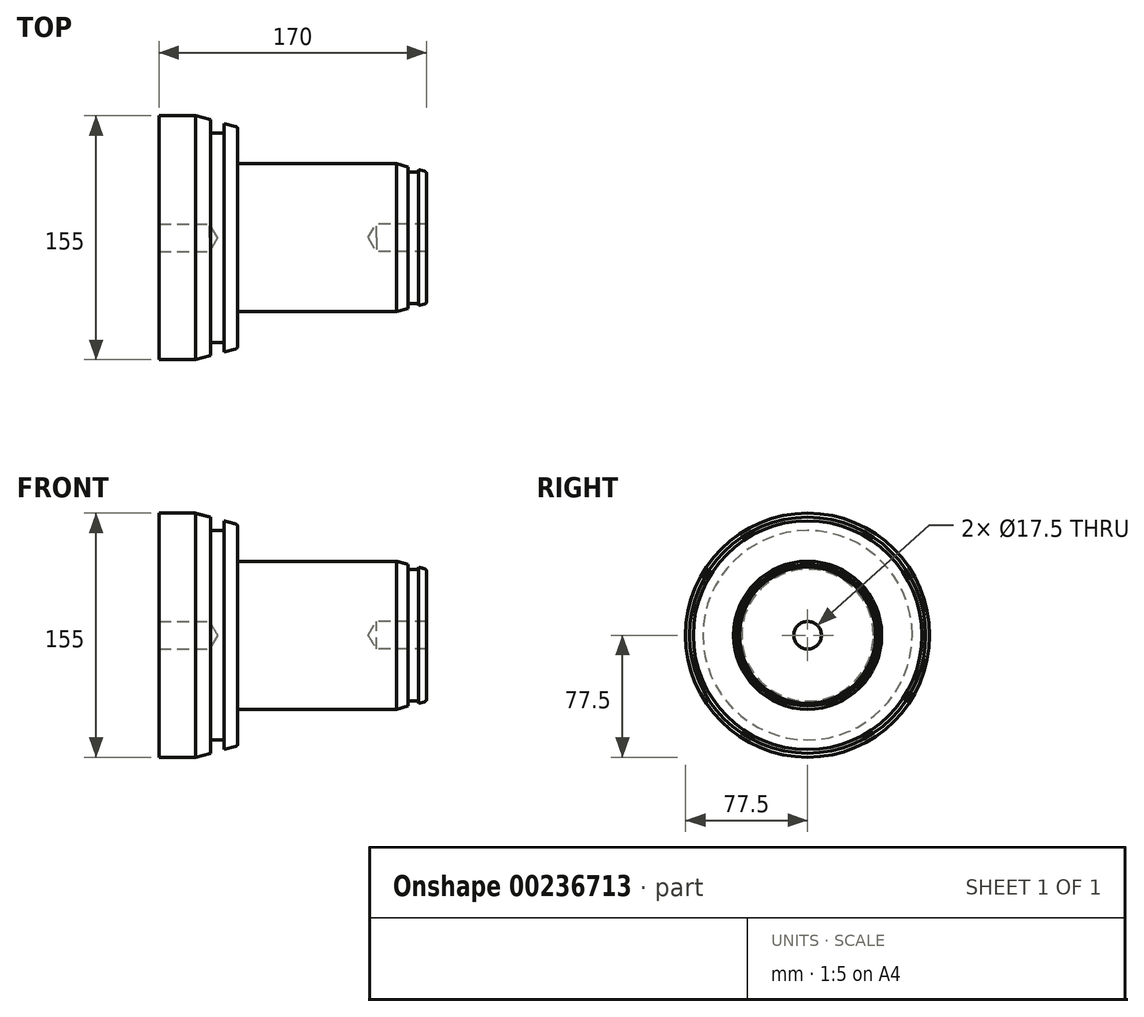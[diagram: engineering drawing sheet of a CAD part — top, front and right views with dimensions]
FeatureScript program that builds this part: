
annotation { "Feature Type Name" : "Feature", "Feature Type Description" : "" }
export const myFeature = defineFeature(function(context is Context, id is Id, definition is map)
    precondition{}
    {
        {
            var Q0;
            Q0=qCreatedBy(makeId("Front.planeOp"),FACE);
            var sketch = newSketch(context, id + "F0", { "sketchPlane" : qUnion([Q0])});
            skLineSegment(sketch, "E0", {"start": v(0, 0) * mm, "end": v(170, 0) * mm});
            skLineSegment(sketch, "E1", {"start": v(0, 0) * mm, "end": v(0, 77.5) * mm});
            skLineSegment(sketch, "E2", {"start": v(0, 77.5) * mm, "end": v(23.18, 77.5) * mm});
            skLineSegment(sketch, "E3", {"start": v(23.18, 77.5) * mm, "end": v(32.6, 74.98) * mm});
            skLineSegment(sketch, "E4", {"start": v(50, 68.78) * mm, "end": v(50, 48) * mm});
            skLineSegment(sketch, "E5", {"start": v(51, 47) * mm, "end": v(150.74, 47) * mm});
            skLineSegment(sketch, "E6", {"start": v(158.25, 44.99) * mm, "end": v(158.25, 41.84) * mm});
            skLineSegment(sketch, "E7", {"start": v(158.25, 41.84) * mm, "end": v(164.75, 41.84) * mm});
            skLineSegment(sketch, "E8", {"start": v(164.75, 41.84) * mm, "end": v(164.75, 43.25) * mm});
            skLineSegment(sketch, "E9", {"start": v(170, 40.3) * mm, "end": v(170, 0) * mm});
            skLineSegment(sketch, "E10", {"start": v(41.4, 72.62) * mm, "end": v(41.4, 66.46) * mm});
            skLineSegment(sketch, "E11", {"start": v(41.4, 66.46) * mm, "end": v(32.6, 66.46) * mm});
            skLineSegment(sketch, "E12", {"start": v(32.6, 66.46) * mm, "end": v(32.6, 74.98) * mm});
            skLineSegment(sketch, "E13.trimOffspring", {"start": v(41.4, 72.62) * mm, "end": v(48.52, 70.71) * mm});
            skPoint(sketch, "E14.visualSharp", {"position": v(50, 70.31) * mm});
            skArc(sketch, "E14.filletArc", {"start": v(50, 68.78) * mm, "mid": v(49.59, 70) * mm, "end": v(48.52, 70.71) * mm});
            skPoint(sketch, "E15.visualSharp", {"position": v(50, 47) * mm});
            skArc(sketch, "E15.filletArc", {"start": v(50, 48) * mm, "mid": v(50.3, 47.3) * mm, "end": v(51, 47) * mm});
            skLineSegment(sketch, "E16", {"start": v(168.52, 42.24) * mm, "end": v(164.75, 43.25) * mm});
            skLineSegment(sketch, "E17.trimOffspring", {"start": v(158.25, 44.99) * mm, "end": v(150.74, 47) * mm});
            skPoint(sketch, "E18.visualSharp", {"position": v(170, 41.84) * mm});
            skArc(sketch, "E18.filletArc", {"start": v(170, 40.3) * mm, "mid": v(169.59, 41.52) * mm, "end": v(168.52, 42.24) * mm});
            skSolve(sketch);
        }
        {
            var Q0;
            Q0=qSketchRegion(id+"F0",true);
            var Q1;
            Q1=sQuery(id+"F0.wireOp",EDGE,"E0");
            revolve(context, id + "F1", {"surfaceOperationType" : NewSurfaceOperationType.NEW, "entities" : qUnion([Q0]), "axis" : qUnion([Q1]), "revolveType" : RevolveType.FULL});
        }
        {
            var Q0;
            Q0=makeQuery(id+"F1.opRevolve","SWEPT_FACE",FACE,{"disambiguationData":[OSD([sQuery(id+"F0.wireOp",EDGE,"E1")])]});
            var sketch = newSketch(context, id + "F2", { "sketchPlane" : qUnion([Q0])});
            skPoint(sketch, "E19", {"position": v(0, 0) * mm});
            skSolve(sketch);
        }
        {
            var Q0;
            Q0=sQuery(id+"F2.wireOp",VERTEX,"E19");
            var Q1;
            Q1=makeQuery(id+"F1.opRevolve","SWEPT_BODY",BODY,{"disambiguationData":[OSD([sQuery(id+"F0.wireOp",EDGE,"E0"),sQuery(id+"F0.wireOp",EDGE,"E1"),sQuery(id+"F0.wireOp",EDGE,"E2"),sQuery(id+"F0.wireOp",EDGE,"E3"),sQuery(id+"F0.wireOp",EDGE,"E4"),sQuery(id+"F0.wireOp",EDGE,"E5"),sQuery(id+"F0.wireOp",EDGE,"E6"),sQuery(id+"F0.wireOp",EDGE,"E7"),sQuery(id+"F0.wireOp",EDGE,"E8"),sQuery(id+"F0.wireOp",EDGE,"E9"),sQuery(id+"F0.wireOp",EDGE,"E10"),sQuery(id+"F0.wireOp",EDGE,"E11"),sQuery(id+"F0.wireOp",EDGE,"E12"),sQuery(id+"F0.wireOp",EDGE,"E13.trimOffspring"),sQuery(id+"F0.wireOp",EDGE,"E14.filletArc"),sQuery(id+"F0.wireOp",EDGE,"E15.filletArc"),sQuery(id+"F0.wireOp",EDGE,"E16"),sQuery(id+"F0.wireOp",EDGE,"E17.trimOffspring"),sQuery(id+"F0.wireOp",EDGE,"E18.filletArc")])]});
            hole(context, id + "F3", {"style" : HoleStyle.SIMPLE, "endStyle" : HoleEndStyle.BLIND, "standardTappedOrClearance" : lookupTablePath({ "standard" : "ISO", "fit" : "Normal", "size" : "M16", "type" : "Clearance" }), "standardBlindInLast" : lookupTablePath({ "fit" : "Standard", "standard" : "ISO", "size" : "M16", "type" : "Clearance" }), "holeDiameter" : 17.5 * mm, "majorDiameter" : 5 * mm, "holeDepth" : 32 * mm, "isTappedThrough" : true, "tappedDepth" : 28 * mm, "tapClearance" : 3, "locations" : qUnion([Q0]), "scope" : qUnion([Q1])});
        }
        {
            var Q0;
            Q0=makeQuery(id+"F1.opRevolve","SWEPT_FACE",FACE,{"disambiguationData":[OSD([sQuery(id+"F0.wireOp",EDGE,"E9")])]});
            var sketch = newSketch(context, id + "F4", { "sketchPlane" : qUnion([Q0])});
            skPoint(sketch, "E20", {"position": v(0, 0) * mm});
            skSolve(sketch);
        }
        {
            var Q0;
            Q0=sQuery(id+"F4.wireOp",VERTEX,"E20");
            var Q1;
            Q1=makeQuery(id+"F1.opRevolve","SWEPT_BODY",BODY,{"disambiguationData":[OSD([sQuery(id+"F0.wireOp",EDGE,"E0"),sQuery(id+"F0.wireOp",EDGE,"E1"),sQuery(id+"F0.wireOp",EDGE,"E2"),sQuery(id+"F0.wireOp",EDGE,"E3"),sQuery(id+"F0.wireOp",EDGE,"E4"),sQuery(id+"F0.wireOp",EDGE,"E5"),sQuery(id+"F0.wireOp",EDGE,"E6"),sQuery(id+"F0.wireOp",EDGE,"E7"),sQuery(id+"F0.wireOp",EDGE,"E8"),sQuery(id+"F0.wireOp",EDGE,"E9"),sQuery(id+"F0.wireOp",EDGE,"E10"),sQuery(id+"F0.wireOp",EDGE,"E11"),sQuery(id+"F0.wireOp",EDGE,"E12"),sQuery(id+"F0.wireOp",EDGE,"E13.trimOffspring"),sQuery(id+"F0.wireOp",EDGE,"E14.filletArc"),sQuery(id+"F0.wireOp",EDGE,"E15.filletArc"),sQuery(id+"F0.wireOp",EDGE,"E16"),sQuery(id+"F0.wireOp",EDGE,"E17.trimOffspring"),sQuery(id+"F0.wireOp",EDGE,"E18.filletArc")])]});
            hole(context, id + "F5", {"style" : HoleStyle.SIMPLE, "endStyle" : HoleEndStyle.BLIND, "standardTappedOrClearance" : lookupTablePath({ "standard" : "ISO", "fit" : "Normal", "size" : "M16", "type" : "Clearance" }), "standardBlindInLast" : lookupTablePath({ "fit" : "Standard", "standard" : "ISO", "size" : "M16", "type" : "Clearance" }), "holeDiameter" : 17.5 * mm, "majorDiameter" : 5 * mm, "holeDepth" : 32 * mm, "isTappedThrough" : true, "tappedDepth" : 28 * mm, "tapClearance" : 3, "locations" : qUnion([Q0]), "scope" : qUnion([Q1])});
        }
    });
